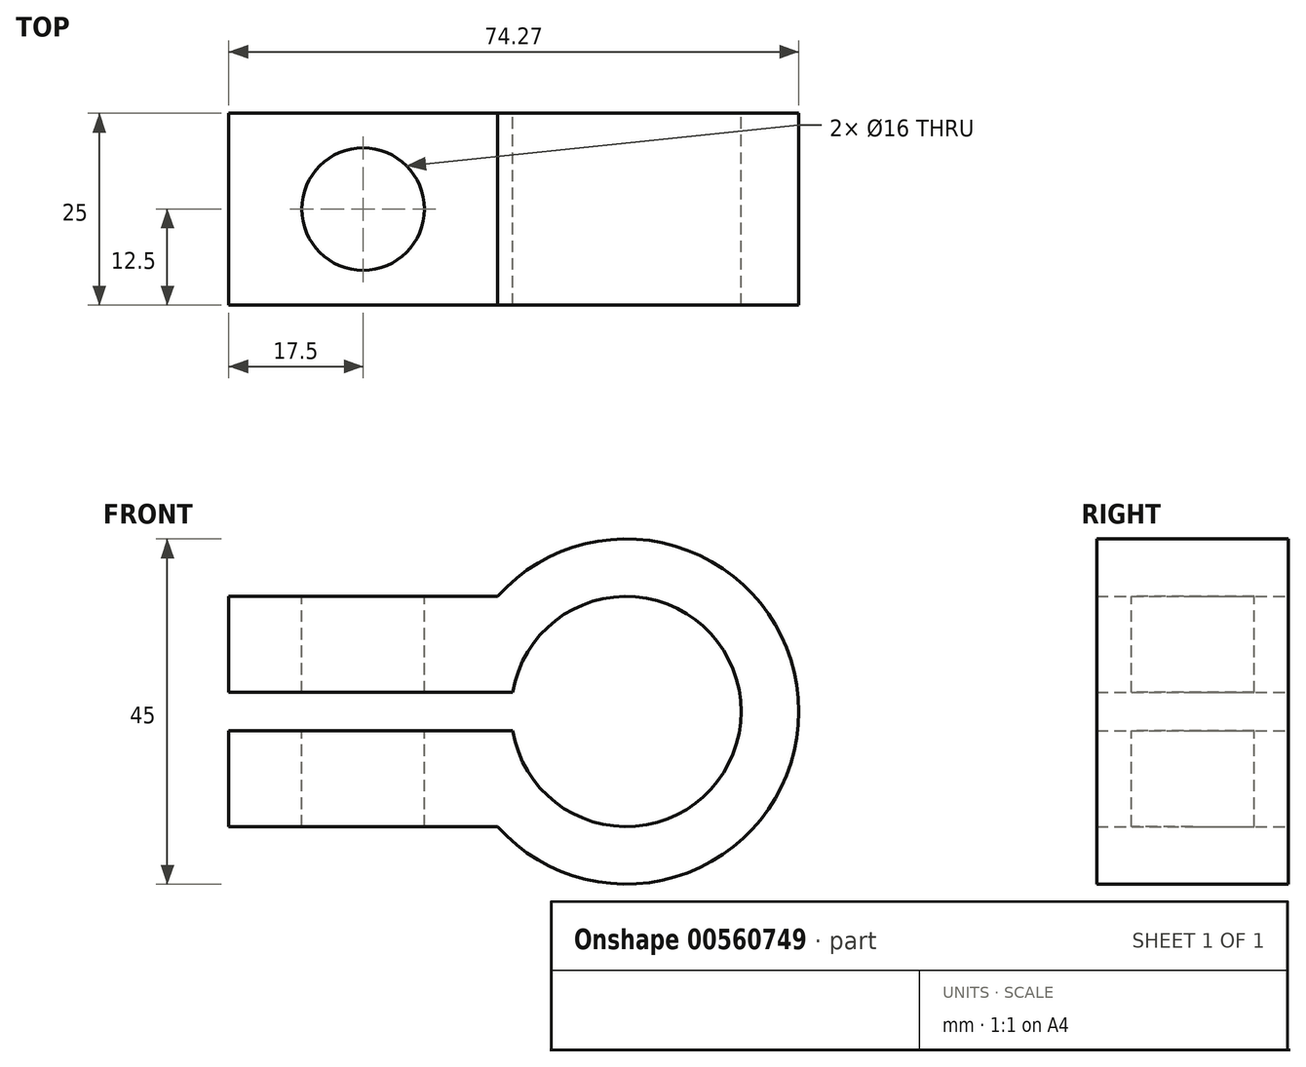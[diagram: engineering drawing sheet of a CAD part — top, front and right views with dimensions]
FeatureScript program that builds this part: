
annotation { "Feature Type Name" : "Feature", "Feature Type Description" : "" }
export const myFeature = defineFeature(function(context is Context, id is Id, definition is map)
    precondition{}
    {
        {
            var Q0;
            Q0=qCreatedBy(makeId("Front.planeOp"),FACE);
            var sketch = newSketch(context, id + "F0", { "sketchPlane" : qUnion([Q0])});
            skCircle(sketch, "E0", {"center": v(0, 0) * mm, "radius": 15 * mm});
            skCircle(sketch, "E1", {"center": v(0, 0) * mm, "radius": 22.5 * mm});
            skLineSegment(sketch, "E2", {"start": v(-16.77, 15) * mm, "end": v(-51.77, 15) * mm});
            skLineSegment(sketch, "E3", {"start": v(-51.77, 15) * mm, "end": v(-51.77, 2.5) * mm});
            skLineSegment(sketch, "E4", {"start": v(-51.77, 2.5) * mm, "end": v(-14.8, 2.5) * mm});
            skLineSegment(sketch, "E5", {"start": v(-16.77, -15) * mm, "end": v(-51.77, -15) * mm});
            skLineSegment(sketch, "E6", {"start": v(-51.77, -15) * mm, "end": v(-51.77, -2.5) * mm});
            skLineSegment(sketch, "E7", {"start": v(-51.77, -2.5) * mm, "end": v(-14.8, -2.5) * mm});
            skSolve(sketch);
        }
        {
            var Q0;
            {var subQ0=sQuery(id+"F0.wireOp",EDGE,"E2");Q0=makeQuery(id+"F0.imprint","IMPRINT",FACE,{"disambiguationData":[TD([[makeQuery(id+"F0.imprint","IMPRINT",EDGE,{"derivedFrom":subQ0}),1.0]])]});}
            var Q1;
            {var subQ0=sQuery(id+"F0.wireOp",EDGE,"E5");Q1=makeQuery(id+"F0.imprint","IMPRINT",FACE,{"disambiguationData":[TD([[makeQuery(id+"F0.imprint","IMPRINT",EDGE,{"derivedFrom":subQ0}),-1.0]])]});}
            var Q2;
            {var subQ5=sQuery(id+"F0.wireOp",EDGE,"E4");var subQ7=sQuery(id+"F0.wireOp",EDGE,"E0");var subQ9=makeQuery(id+"F0.imprint","INTERSECT",VERTEX,{"derivedFrom":[subQ7,subQ5]});Q2=makeQuery(id+"F0.imprint","IMPRINT",FACE,{"disambiguationData":[TD([[makeQuery(id+"F0.imprint","IMPRINT",EDGE,{"disambiguationData":[TD([[subQ9,1.0]])],"derivedFrom":subQ7}),-1.0]])]});}
            extrude(context, id + "F1", {"entities" : qUnion([Q0, Q1, Q2]), "depth" : 25 * mm, "offsetDistance" : 25 * mm});
        }
        {
            var Q0;
            Q0=makeQuery(id+"F1.opExtrude","SWEPT_FACE",FACE,{"disambiguationData":[OSD([sQuery(id+"F0.wireOp",EDGE,"E2")])]});
            var sketch = newSketch(context, id + "F2", { "sketchPlane" : qUnion([Q0])});
            skCircle(sketch, "E8", {"center": v(-34.27, -12.5) * mm, "radius": 8 * mm});
            skPoint(sketch, "E8.centerSnap0", {"position": v(-34.27, 0) * mm});
            skSolve(sketch);
        }
        {
            var Q0;
            Q0=makeQuery(id+"F2.imprint","IMPRINT",FACE,{"disambiguationData":[TD([[makeQuery(id+"F2.imprint","IMPRINT",EDGE,{"derivedFrom":sQuery(id+"F2.wireOp",EDGE,"E8")}),1.0]])]});
            extrude(context, id + "F3", {"entities" : qUnion([Q0]), "operationType" : NewBodyOperationType.REMOVE, "endBound" : BoundingType.THROUGH_ALL, "oppositeDirection" : true, "depth" : 25 * mm, "offsetDistance" : 25 * mm});
        }
    });
